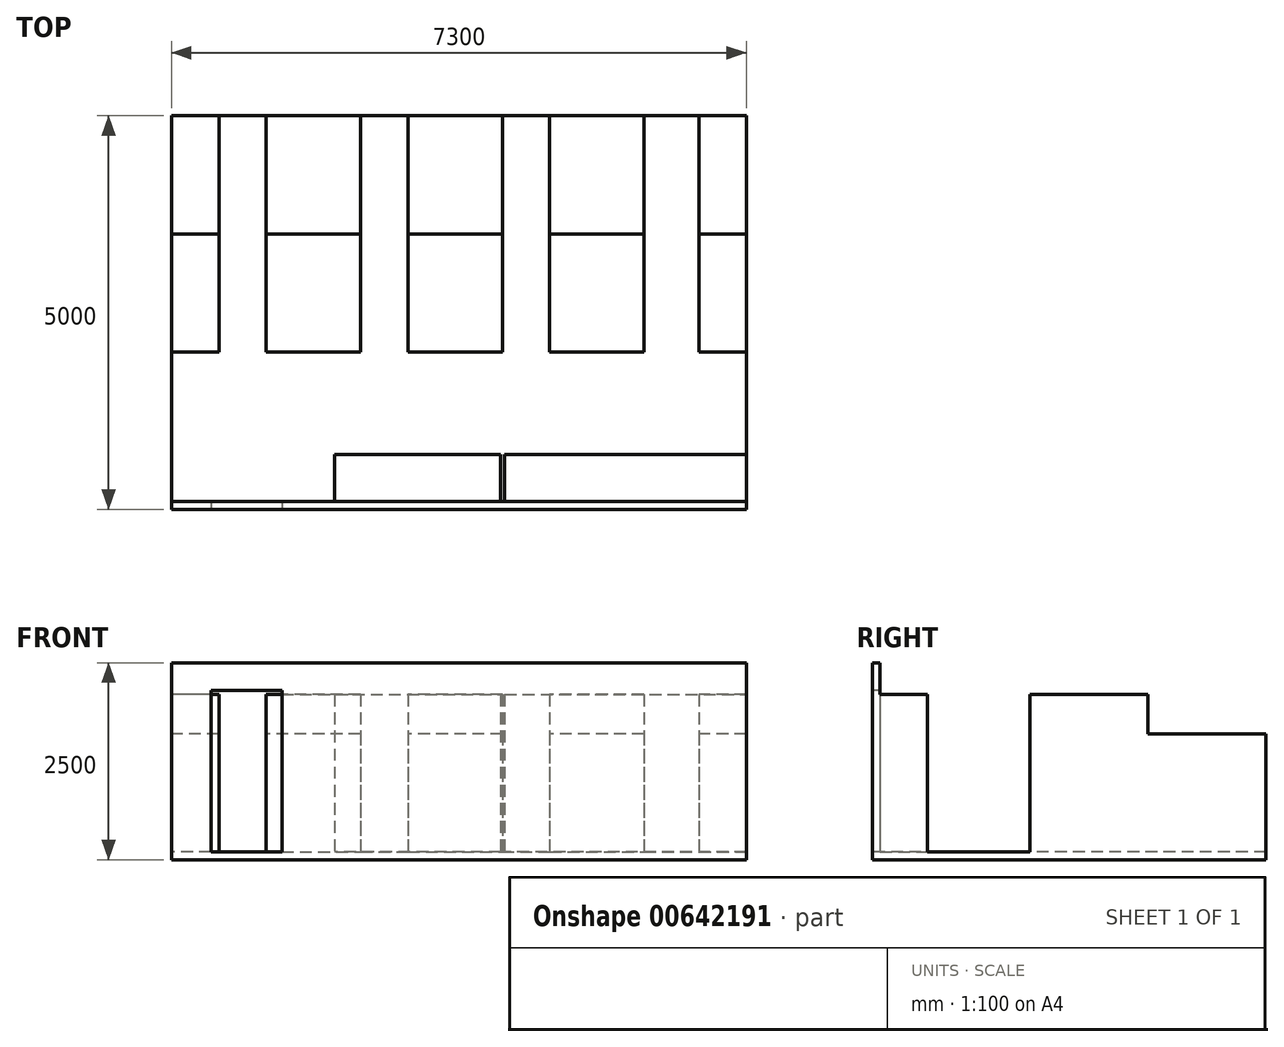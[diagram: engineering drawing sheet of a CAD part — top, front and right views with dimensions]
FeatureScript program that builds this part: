
annotation { "Feature Type Name" : "Feature", "Feature Type Description" : "" }
export const myFeature = defineFeature(function(context is Context, id is Id, definition is map)
    precondition{}
    {
        {
            var Q0;
            Q0=qCreatedBy(makeId("Top.planeOp"),FACE);
            var sketch = newSketch(context, id + "F0", { "sketchPlane" : qUnion([Q0])});
            skLineSegment(sketch, "E0.bottom", {"start": v(-3654.07, 3477.17) * mm, "end": v(3645.93, 3477.17) * mm});
            skLineSegment(sketch, "E0.top", {"start": v(-3654.07, -1522.83) * mm, "end": v(3645.93, -1522.83) * mm});
            skLineSegment(sketch, "E0.left", {"start": v(-3654.07, 3477.17) * mm, "end": v(-3654.07, -1522.83) * mm});
            skLineSegment(sketch, "E0.right", {"start": v(3645.93, 3477.17) * mm, "end": v(3645.93, -1522.83) * mm});
            skSolve(sketch);
        }
        {
            var Q0;
            Q0=makeQuery(id+"F0.imprint","IMPRINT",FACE,{"disambiguationData":[TD([[makeQuery(id+"F0.imprint","IMPRINT",EDGE,{"derivedFrom":sQuery(id+"F0.wireOp",EDGE,"E0.bottom")}),-1.0]])]});
            extrude(context, id + "F1", {"entities" : qUnion([Q0]), "depth" : 100 * mm, "offsetDistance" : 25 * mm});
        }
        {
            var Q0;
            Q0=makeQuery(id+"F1.opExtrude","CAP_FACE",FACE,{"disambiguationData":[OSD([sQuery(id+"F0.wireOp",EDGE,"E0.bottom"),sQuery(id+"F0.wireOp",EDGE,"E0.top"),sQuery(id+"F0.wireOp",EDGE,"E0.left"),sQuery(id+"F0.wireOp",EDGE,"E0.right")])],"isStart":false});
            var sketch = newSketch(context, id + "F2", { "sketchPlane" : qUnion([Q0])});
            skLineSegment(sketch, "E1", {"start": v(-3054.07, 3477.17) * mm, "end": v(-3054.07, 477.17) * mm});
            skLineSegment(sketch, "E2", {"start": v(-3054.07, 477.17) * mm, "end": v(-3654.07, 477.17) * mm});
            skLineSegment(sketch, "E3.bottom", {"start": v(-2454.07, 3477.17) * mm, "end": v(-1254.07, 3477.17) * mm});
            skLineSegment(sketch, "E3.top", {"start": v(-2454.07, 477.17) * mm, "end": v(-1254.07, 477.17) * mm});
            skLineSegment(sketch, "E3.left", {"start": v(-2454.07, 3477.17) * mm, "end": v(-2454.07, 477.17) * mm});
            skLineSegment(sketch, "E3.right", {"start": v(-1254.07, 3477.17) * mm, "end": v(-1254.07, 477.17) * mm});
            skLineSegment(sketch, "E4.bottom", {"start": v(-654.07, 3477.17) * mm, "end": v(545.93, 3477.17) * mm});
            skLineSegment(sketch, "E4.top", {"start": v(-654.07, 477.17) * mm, "end": v(545.93, 477.17) * mm});
            skLineSegment(sketch, "E4.left", {"start": v(-654.07, 3477.17) * mm, "end": v(-654.07, 477.17) * mm});
            skLineSegment(sketch, "E4.right", {"start": v(545.93, 3477.17) * mm, "end": v(545.93, 477.17) * mm});
            skLineSegment(sketch, "E5.bottom", {"start": v(1145.93, 3477.17) * mm, "end": v(2345.93, 3477.17) * mm});
            skLineSegment(sketch, "E5.top", {"start": v(1145.93, 477.17) * mm, "end": v(2345.93, 477.17) * mm});
            skLineSegment(sketch, "E5.left", {"start": v(1145.93, 3477.17) * mm, "end": v(1145.93, 477.17) * mm});
            skLineSegment(sketch, "E5.right", {"start": v(2345.93, 3477.17) * mm, "end": v(2345.93, 477.17) * mm});
            skLineSegment(sketch, "E6", {"start": v(3045.93, 3477.17) * mm, "end": v(3045.93, 477.17) * mm});
            skLineSegment(sketch, "E7", {"start": v(3045.93, 477.17) * mm, "end": v(3645.93, 477.17) * mm});
            skSolve(sketch);
        }
        {
            var Q0;
            {var subQ0=sQuery(id+"F2.wireOp",EDGE,"E1");Q0=makeQuery(id+"F2.imprint","IMPRINT",FACE,{"disambiguationData":[TD([[makeQuery(id+"F2.imprint","IMPRINT",EDGE,{"derivedFrom":subQ0}),-1.0]])]});}
            var Q1;
            Q1=makeQuery(id+"F2.imprint","IMPRINT",FACE,{"disambiguationData":[TD([[makeQuery(id+"F2.imprint","IMPRINT",EDGE,{"derivedFrom":sQuery(id+"F2.wireOp",EDGE,"E3.bottom")}),-1.0]])]});
            var Q2;
            Q2=makeQuery(id+"F2.imprint","IMPRINT",FACE,{"disambiguationData":[TD([[makeQuery(id+"F2.imprint","IMPRINT",EDGE,{"derivedFrom":sQuery(id+"F2.wireOp",EDGE,"E4.bottom")}),-1.0]])]});
            var Q3;
            Q3=makeQuery(id+"F2.imprint","IMPRINT",FACE,{"disambiguationData":[TD([[makeQuery(id+"F2.imprint","IMPRINT",EDGE,{"derivedFrom":sQuery(id+"F2.wireOp",EDGE,"E5.bottom")}),-1.0]])]});
            var Q4;
            {var subQ0=sQuery(id+"F2.wireOp",EDGE,"E6");Q4=makeQuery(id+"F2.imprint","IMPRINT",FACE,{"disambiguationData":[TD([[makeQuery(id+"F2.imprint","IMPRINT",EDGE,{"derivedFrom":subQ0}),1.0]])]});}
            extrude(context, id + "F3", {"entities" : qUnion([Q0, Q1, Q2, Q3, Q4]), "operationType" : NewBodyOperationType.ADD, "depth" : 2000 * mm, "offsetDistance" : 25 * mm});
        }
        {
            var Q0;
            {var subQ0=sQuery(id+"F0.wireOp",EDGE,"E0.left");Q0=makeQuery(id+"F3.boolean.opBoolean","MERGE",FACE,{"derivedFrom":[makeQuery(id+"F1.opExtrude","SWEPT_FACE",FACE,{"disambiguationData":[OSD([subQ0])]}),makeQuery(id+"F3.opExtrude","SWEPT_FACE",FACE,{"disambiguationData":[OSD([subQ0])]})]});}
            var sketch = newSketch(context, id + "F4", { "sketchPlane" : qUnion([Q0])});
            skLineSegment(sketch, "E8", {"start": v(-3477.17, 1600) * mm, "end": v(-1977.17, 1600) * mm});
            skLineSegment(sketch, "E9", {"start": v(-1977.17, 1600) * mm, "end": v(-1977.17, 2100) * mm});
            skSolve(sketch);
        }
        {
            var Q0;
            {var subQ0=sQuery(id+"F4.wireOp",EDGE,"E8");Q0=makeQuery(id+"F4.imprint","IMPRINT",FACE,{"disambiguationData":[TD([[makeQuery(id+"F4.imprint","IMPRINT",EDGE,{"derivedFrom":subQ0}),1.0]])]});}
            extrude(context, id + "F5", {"entities" : qUnion([Q0]), "operationType" : NewBodyOperationType.REMOVE, "oppositeDirection" : true, "depth" : 8000 * mm, "offsetDistance" : 25 * mm});
        }
        {
            var Q0;
            Q0=makeQuery(id+"F1.opExtrude","CAP_FACE",FACE,{"disambiguationData":[OSD([sQuery(id+"F0.wireOp",EDGE,"E0.bottom"),sQuery(id+"F0.wireOp",EDGE,"E0.top"),sQuery(id+"F0.wireOp",EDGE,"E0.left"),sQuery(id+"F0.wireOp",EDGE,"E0.right")])],"isStart":false});
            var sketch = newSketch(context, id + "F6", { "sketchPlane" : qUnion([Q0])});
            skLineSegment(sketch, "E10.bottom", {"start": v(-3654.07, -1422.83) * mm, "end": v(3645.93, -1422.83) * mm});
            skLineSegment(sketch, "E10.top", {"start": v(-3654.07, -1522.83) * mm, "end": v(3645.93, -1522.83) * mm});
            skLineSegment(sketch, "E10.left", {"start": v(-3654.07, -1422.83) * mm, "end": v(-3654.07, -1522.83) * mm});
            skLineSegment(sketch, "E10.right", {"start": v(3645.93, -1422.83) * mm, "end": v(3645.93, -1522.83) * mm});
            skSolve(sketch);
        }
        {
            var Q0;
            Q0=makeQuery(id+"F6.imprint","IMPRINT",FACE,{"disambiguationData":[TD([[makeQuery(id+"F6.imprint","IMPRINT",EDGE,{"derivedFrom":sQuery(id+"F6.wireOp",EDGE,"E10.bottom")}),-1.0]])]});
            extrude(context, id + "F7", {"entities" : qUnion([Q0]), "operationType" : NewBodyOperationType.ADD, "depth" : 2400 * mm, "offsetDistance" : 25 * mm});
        }
        {
            var Q0;
            Q0=makeQuery(id+"F7.boolean.opBoolean","MERGE",FACE,{"derivedFrom":[makeQuery(id+"F1.opExtrude","SWEPT_FACE",FACE,{"disambiguationData":[OSD([sQuery(id+"F0.wireOp",EDGE,"E0.top")])]}),makeQuery(id+"F7.opExtrude","SWEPT_FACE",FACE,{"disambiguationData":[OSD([sQuery(id+"F6.wireOp",EDGE,"E10.top")])]})]});
            var sketch = newSketch(context, id + "F8", { "sketchPlane" : qUnion([Q0])});
            skLineSegment(sketch, "E11.bottom", {"start": v(-3154.07, 2150) * mm, "end": v(-2254.07, 2150) * mm});
            skLineSegment(sketch, "E11.top", {"start": v(-3154.07, 100) * mm, "end": v(-2254.07, 100) * mm});
            skLineSegment(sketch, "E11.left", {"start": v(-3154.07, 2150) * mm, "end": v(-3154.07, 100) * mm});
            skLineSegment(sketch, "E11.right", {"start": v(-2254.07, 2150) * mm, "end": v(-2254.07, 100) * mm});
            skSolve(sketch);
        }
        {
            var Q0;
            Q0=makeQuery(id+"F8.imprint","IMPRINT",FACE,{"disambiguationData":[TD([[makeQuery(id+"F8.imprint","IMPRINT",EDGE,{"derivedFrom":sQuery(id+"F8.wireOp",EDGE,"E11.bottom")}),-1.0]])]});
            extrude(context, id + "F9", {"entities" : qUnion([Q0]), "operationType" : NewBodyOperationType.REMOVE, "oppositeDirection" : true, "depth" : 100 * mm, "offsetDistance" : 25 * mm});
        }
        {
            var Q0;
            Q0=makeQuery(id+"F9.boolean.opBoolean","MERGE",FACE,{"derivedFrom":[makeQuery(id+"F1.opExtrude","CAP_FACE",FACE,{"disambiguationData":[OSD([sQuery(id+"F0.wireOp",EDGE,"E0.bottom"),sQuery(id+"F0.wireOp",EDGE,"E0.top"),sQuery(id+"F0.wireOp",EDGE,"E0.left"),sQuery(id+"F0.wireOp",EDGE,"E0.right")])],"isStart":false}),makeQuery(id+"F9.opExtrude","SWEPT_FACE",FACE,{"disambiguationData":[OSD([sQuery(id+"F8.wireOp",EDGE,"E11.top")])]})]});
            var sketch = newSketch(context, id + "F10", { "sketchPlane" : qUnion([Q0])});
            skLineSegment(sketch, "E12.bottom", {"start": v(3645.93, -1422.83) * mm, "end": v(575.93, -1422.83) * mm});
            skLineSegment(sketch, "E12.top", {"start": v(3645.93, -822.83) * mm, "end": v(575.93, -822.83) * mm});
            skLineSegment(sketch, "E12.left", {"start": v(3645.93, -1422.83) * mm, "end": v(3645.93, -822.83) * mm});
            skLineSegment(sketch, "E12.right", {"start": v(575.93, -1422.83) * mm, "end": v(575.93, -822.83) * mm});
            skSolve(sketch);
        }
        {
            var Q0;
            {var subQ6=sQuery(id+"F10.wireOp",EDGE,"E12.top");Q0=makeQuery(id+"F10.imprint","IMPRINT",FACE,{"disambiguationData":[TD([[makeQuery(id+"F10.imprint","IMPRINT",EDGE,{"derivedFrom":subQ6}),-1.0]])]});}
            var sketch = newSketch(context, id + "F11", { "sketchPlane" : qUnion([Q0])});
            skLineSegment(sketch, "E13.0", {"start": v(575.93, -1422.83) * mm, "end": v(575.93, -822.83) * mm});
            skLineSegment(sketch, "E14", {"start": v(575.93, -822.83) * mm, "end": v(-1584.07, -822.83) * mm});
            skLineSegment(sketch, "E15", {"start": v(-1584.07, -822.83) * mm, "end": v(-1584.07, -1422.83) * mm});
            skLineSegment(sketch, "E16.0", {"start": v(525.93, -1422.83) * mm, "end": v(525.93, -822.83) * mm});
            skSolve(sketch);
        }
        {
            var Q0;
            Q0=makeQuery(id+"F10.imprint","IMPRINT",FACE,{"disambiguationData":[TD([[makeQuery(id+"F10.imprint","IMPRINT",EDGE,{"derivedFrom":sQuery(id+"F10.wireOp",EDGE,"E12.bottom")}),1.0]])]});
            var Q1;
            {var subQ0=sQuery(id+"F11.wireOp",EDGE,"E15");Q1=makeQuery(id+"F11.imprint","IMPRINT",FACE,{"disambiguationData":[TD([[makeQuery(id+"F11.imprint","IMPRINT",EDGE,{"derivedFrom":subQ0}),1.0]])]});}
            extrude(context, id + "F12", {"entities" : qUnion([Q0, Q1]), "operationType" : NewBodyOperationType.ADD, "depth" : 2000 * mm, "offsetDistance" : 25 * mm});
        }
    });
